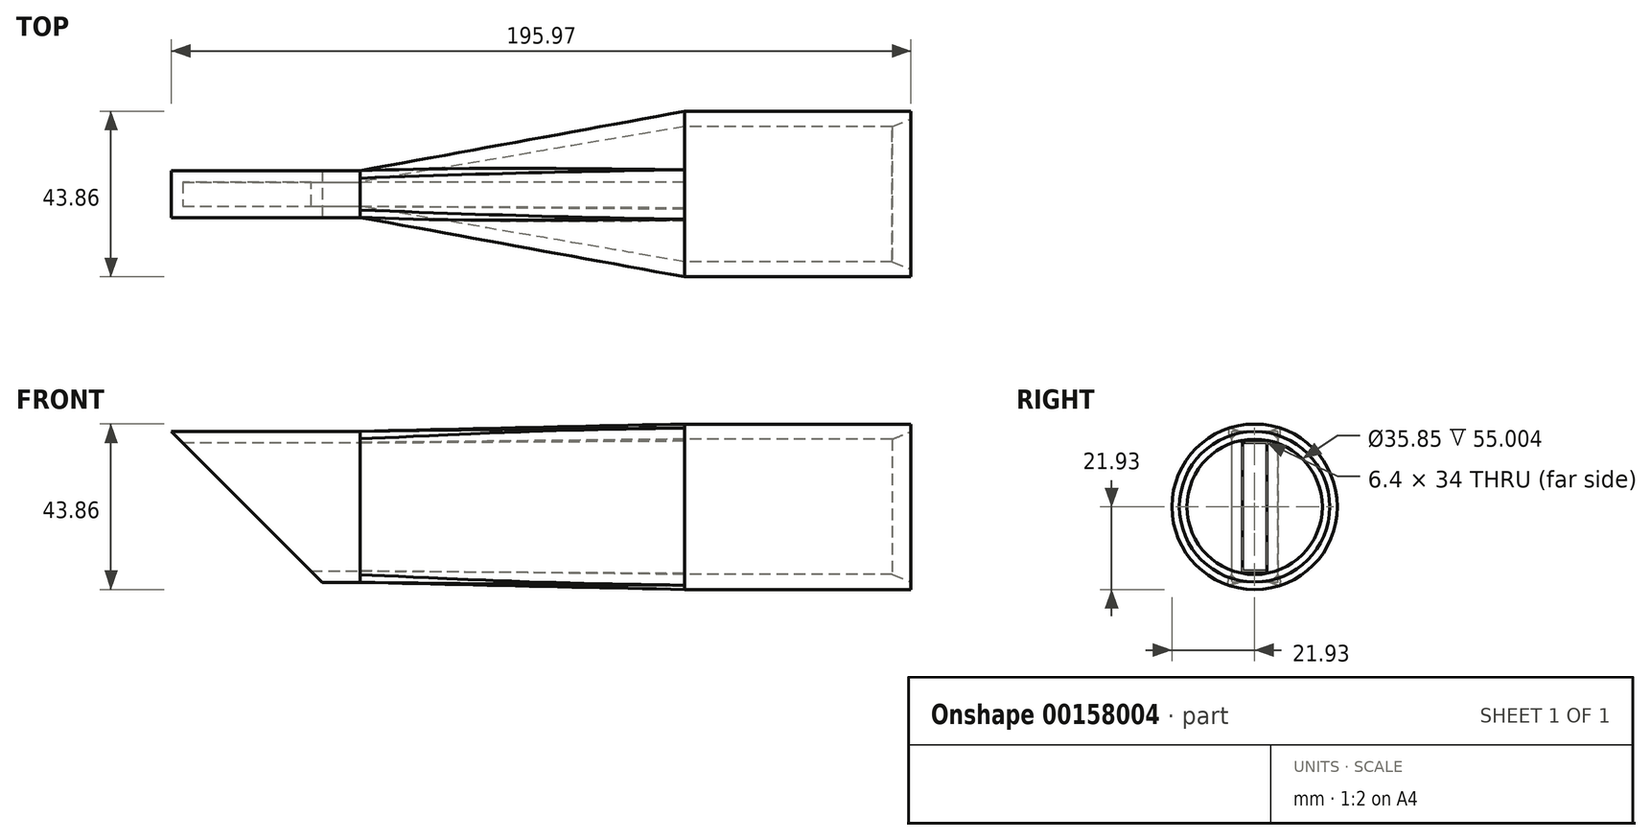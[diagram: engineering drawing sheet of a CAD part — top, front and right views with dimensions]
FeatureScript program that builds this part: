
annotation { "Feature Type Name" : "Feature", "Feature Type Description" : "" }
export const myFeature = defineFeature(function(context is Context, id is Id, definition is map)
    precondition{}
    {
        {
            var Q0;
            Q0=qCreatedBy(makeId("Front.planeOp"),FACE);
            var sketch = newSketch(context, id + "F0", { "sketchPlane" : qUnion([Q0])});
            skLineSegment(sketch, "E0", {"start": v(-54.03, 0) * mm, "end": v(-4.03, 0) * mm, "construction": true});
            skLineSegment(sketch, "E1", {"start": v(-4.03, 0) * mm, "end": v(-4.03, 17.93) * mm, "construction": true});
            skLineSegment(sketch, "E2", {"start": v(-54.04, 0.55) * mm, "end": v(-54.04, 17.93) * mm, "construction": true});
            skLineSegment(sketch, "E3", {"start": v(-54.04, 17.92) * mm, "end": v(5.97, 17.93) * mm});
            skLineSegment(sketch, "E4", {"start": v(-54.04, 17.93) * mm, "end": v(-54.04, 21.92) * mm});
            skLineSegment(sketch, "E5", {"start": v(5.97, 17.93) * mm, "end": v(5.97, 21.93) * mm});
            skLineSegment(sketch, "E6", {"start": v(5.97, 21.93) * mm, "end": v(-54.04, 21.92) * mm});
            skSolve(sketch);
        }
        {
            var Q0;
            Q0=makeQuery(id+"F0.imprint","IMPRINT",FACE,{"disambiguationData":[TD([[makeQuery(id+"F0.imprint","IMPRINT",EDGE,{"derivedFrom":sQuery(id+"F0.wireOp",EDGE,"E3")}),1.0]])]});
            var Q1;
            Q1=sQuery(id+"F0.wireOp",EDGE,"E0");
            revolve(context, id + "F1", {"entities" : qUnion([Q0]), "axis" : qUnion([Q1]), "revolveType" : RevolveType.FULL});
        }
        {
            var Q0;
            Q0=makeQuery(id+"F1.opRevolve","SWEPT_EDGE",EDGE,{"disambiguationData":[OSD([sQuery(id+"F0.wireOp",EDGE,"E3"),sQuery(id+"F0.wireOp",EDGE,"E5")])]});
            chamfer(context, id + "F2", {"entities" : qUnion([Q0]), "chamferType" : ChamferType.TWO_OFFSETS, "width1" : 2 * mm, "oppositeDirection" : false, "width2" : 5 * mm, "tangentPropagation" : true});
        }
        {
            var Q0;
            Q0=qCreatedBy(makeId("Right.planeOp"),FACE);
            cPlane(context, id + "F3", {"entities" : qUnion([Q0]), "cplaneType" : CPlaneType.OFFSET, "offset" : 140 * mm, "oppositeDirection" : true, "width" : 150 * mm, "height" : 150 * mm});
        }
        {
            var Q0;
            Q0=qCreatedBy(id+"F3.planeOp",FACE);
            var sketch = newSketch(context, id + "F4", { "sketchPlane" : qUnion([Q0])});
            skPoint(sketch, "E7.0", {"position": v(0, 0) * mm});
            skLineSegment(sketch, "E8.bottom", {"start": v(6.2, 20) * mm, "end": v(-6.2, 20) * mm});
            skLineSegment(sketch, "E8.top", {"start": v(6.2, -20) * mm, "end": v(-6.2, -20) * mm});
            skLineSegment(sketch, "E8.left", {"start": v(6.2, 20) * mm, "end": v(6.2, -20) * mm});
            skLineSegment(sketch, "E8.right", {"start": v(-6.2, 20) * mm, "end": v(-6.2, -20) * mm});
            skLineSegment(sketch, "E9.0", {"start": v(3.2, 17) * mm, "end": v(-3.2, 17) * mm});
            skLineSegment(sketch, "E9.1", {"start": v(3.2, 17) * mm, "end": v(3.2, -17) * mm});
            skLineSegment(sketch, "E9.2", {"start": v(3.2, -17) * mm, "end": v(-3.2, -17) * mm});
            skLineSegment(sketch, "E9.3", {"start": v(-3.2, 17) * mm, "end": v(-3.2, -17) * mm});
            skSolve(sketch);
        }
        {
            var Q0;
            Q0=makeQuery(id+"F1.opRevolve","SWEPT_FACE",FACE,{"disambiguationData":[OSD([sQuery(id+"F0.wireOp",EDGE,"E4")])]});
            var sketch = newSketch(context, id + "F5", { "sketchPlane" : qUnion([Q0])});
            skArc(sketch, "E10", {"start": v(-6.45, 20.96) * mm, "mid": v(-21.92, 0.06) * mm, "end": v(-6.57, -20.92) * mm});
            skArc(sketch, "E11", {"start": v(6.7, 20.88) * mm, "mid": v(0.13, 21.92) * mm, "end": v(-6.45, 20.96) * mm});
            skArc(sketch, "E12", {"start": v(-6.57, -20.92) * mm, "mid": v(0.26, -21.92) * mm, "end": v(7.06, -20.76) * mm});
            skArc(sketch, "E13", {"start": v(7.06, -20.76) * mm, "mid": v(21.92, 0.2) * mm, "end": v(6.7, 20.88) * mm});
            skArc(sketch, "E14", {"start": v(3.93, 17.49) * mm, "mid": v(0.31, 17.92) * mm, "end": v(-3.32, 17.62) * mm});
            skArc(sketch, "E15", {"start": v(-3.32, 17.62) * mm, "mid": v(-17.92, -0.02) * mm, "end": v(-3.28, -17.62) * mm});
            skArc(sketch, "E16", {"start": v(-3.28, -17.62) * mm, "mid": v(0.15, -17.92) * mm, "end": v(3.57, -17.57) * mm});
            skArc(sketch, "E17", {"start": v(3.57, -17.57) * mm, "mid": v(17.92, -0.19) * mm, "end": v(3.93, 17.49) * mm});
            skSolve(sketch);
        }
        {
            var Q0;
            Q0=makeQuery(id+"F4.imprint","IMPRINT",FACE,{"disambiguationData":[TD([[makeQuery(id+"F4.imprint","IMPRINT",EDGE,{"derivedFrom":sQuery(id+"F4.wireOp",EDGE,"E9.0")}),1.0]])]});
            var Q1;
            Q1=makeQuery(id+"F5.imprint","IMPRINT",FACE,{"disambiguationData":[TD([[makeQuery(id+"F5.imprint","IMPRINT",EDGE,{"derivedFrom":sQuery(id+"F5.wireOp",EDGE,"E14")}),1.0]])]});
            loft(context, id + "F6", {"sheetProfilesArray" : [{ "sheetProfileEntities" : qUnion([Q0]) }, { "sheetProfileEntities" : qUnion([Q1]) }]});
        }
        {
            var Q0;
            Q0=qCreatedBy(id+"F3.planeOp",FACE);
            var sketch = newSketch(context, id + "F7", { "sketchPlane" : qUnion([Q0])});
            skLineSegment(sketch, "E18.0", {"start": v(6.2, 20) * mm, "end": v(-6.2, 20) * mm});
            skLineSegment(sketch, "E19.0", {"start": v(6.2, 20) * mm, "end": v(6.2, -20) * mm});
            skLineSegment(sketch, "E20.0", {"start": v(-6.2, 20) * mm, "end": v(-6.2, -20) * mm});
            skLineSegment(sketch, "E21.0", {"start": v(6.2, -20) * mm, "end": v(-6.2, -20) * mm});
            skSolve(sketch);
        }
        {
            var Q0;
            Q0=makeQuery(id+"F5.imprint","IMPRINT",FACE,{"disambiguationData":[TD([[makeQuery(id+"F5.imprint","IMPRINT",EDGE,{"derivedFrom":sQuery(id+"F5.wireOp",EDGE,"E14")}),1.0]])]});
            var sketch = newSketch(context, id + "F8", { "sketchPlane" : qUnion([Q0])});
            skArc(sketch, "E22.0", {"start": v(-6.45, 20.96) * mm, "mid": v(-21.92, 0.06) * mm, "end": v(-6.57, -20.92) * mm});
            skArc(sketch, "E23.0", {"start": v(6.7, 20.88) * mm, "mid": v(0.13, 21.92) * mm, "end": v(-6.45, 20.96) * mm});
            skArc(sketch, "E24.0", {"start": v(7.06, -20.76) * mm, "mid": v(21.92, 0.2) * mm, "end": v(6.7, 20.88) * mm});
            skArc(sketch, "E25.0", {"start": v(-6.57, -20.92) * mm, "mid": v(0.26, -21.92) * mm, "end": v(7.06, -20.76) * mm});
            skSolve(sketch);
        }
        {
            var Q1;
            Q1=makeQuery(id+"F7.imprint","IMPRINT",FACE,{"disambiguationData":[TD([[makeQuery(id+"F7.imprint","IMPRINT",EDGE,{"derivedFrom":sQuery(id+"F7.wireOp",EDGE,"E18.0")}),1.0]])]});
            var Q2;
            Q2 = qSketchRegion(id + "F8", true);
            loft(context, id + "F9", {"sheetProfilesArray" : [{ "sheetProfileEntities" : qUnion([Q1]) }, { "sheetProfileEntities" : qUnion([Q2]) }]});
        }
        {
            var Q0;
            Q0=makeQuery(id+"F6.opLoft","SWEPT_BODY",BODY,{"disambiguationData":[OSD([makeQuery(id+"F4.imprint","IMPRINT",FACE,{"disambiguationData":[TD([[makeQuery(id+"F4.imprint","IMPRINT",EDGE,{"derivedFrom":sQuery(id+"F4.wireOp",EDGE,"E9.0")}),1.0]])]}),makeQuery(id+"F5.imprint","IMPRINT",FACE,{"disambiguationData":[TD([[makeQuery(id+"F5.imprint","IMPRINT",EDGE,{"derivedFrom":sQuery(id+"F5.wireOp",EDGE,"E14")}),1.0]])]})])]});
            var Q1;
            Q1=makeQuery(id+"F9.opLoft","SWEPT_BODY",BODY,{"disambiguationData":[OSD([makeQuery(id+"F7.imprint","IMPRINT",FACE,{"disambiguationData":[TD([[makeQuery(id+"F7.imprint","IMPRINT",EDGE,{"derivedFrom":sQuery(id+"F7.wireOp",EDGE,"E18.0")}),1.0]])]}),makeQuery(id+"F8.imprint","IMPRINT",FACE,{"disambiguationData":[TD([[makeQuery(id+"F8.imprint","IMPRINT",EDGE,{"derivedFrom":sQuery(id+"F8.wireOp",EDGE,"E22.0")}),1.0]])]})])]});
            booleanBodies(context, id + "F10", {"operationType" : BooleanOperationType.SUBTRACTION, "tools" : qUnion([Q0]), "targets" : qUnion([Q1])});
        }
        {
            var Q0;
            Q0=makeQuery(id+"F9.opLoft","CAP_FACE",FACE,{"disambiguationData":[OSD([makeQuery(id+"F7.imprint","IMPRINT",FACE,{"disambiguationData":[TD([[makeQuery(id+"F7.imprint","IMPRINT",EDGE,{"derivedFrom":sQuery(id+"F7.wireOp",EDGE,"E18.0")}),1.0]])]})])],"isStart":true});
            extrude(context, id + "F11", {"entities" : qUnion([Q0]), "depth" : 50 * mm});
        }
        {
            var Q0;
            Q0=makeQuery(id+"F11.opExtrude","SWEPT_FACE",FACE,{"disambiguationData":[OSD([sQuery(id+"F7.wireOp",EDGE,"E18.0"),sQuery(id+"F7.wireOp",EDGE,"E20.0"),sQuery(id+"F7.wireOp",EDGE,"E21.0")])]});
            var sketch = newSketch(context, id + "F12", { "sketchPlane" : qUnion([Q0])});
            skLineSegment(sketch, "E26.0", {"start": v(-190, 20) * mm, "end": v(-190, -20) * mm});
            skFitSpline(sketch, "E27.0", {"points": [v(-210, 20) * mm, v(-193.33, 20) * mm, v(-176.67, 20) * mm, v(-160, 20) * mm]});
            skFitSpline(sketch, "E28.0", {"points": [v(-210, -20) * mm, v(-193.33, -20) * mm, v(-176.67, -20) * mm, v(-160, -20) * mm]});
            skLineSegment(sketch, "E29", {"start": v(-190, 20) * mm, "end": v(-150, -20) * mm});
            skSolve(sketch);
        }
        {
            var Q0;
            {var subQ0=sQuery(id+"F12.wireOp",EDGE,"E26.0");Q0=makeQuery(id+"F12.imprint","IMPRINT",FACE,{"disambiguationData":[TD([[makeQuery(id+"F12.imprint","IMPRINT",EDGE,{"derivedFrom":subQ0}),1.0]])]});}
            extrude(context, id + "F13", {"entities" : qUnion([Q0]), "operationType" : NewBodyOperationType.REMOVE, "oppositeDirection" : true, "depth" : 25 * mm, "symmetric" : true});
        }
        {
            var Q0;
            Q0=makeQuery(id+"F13.boolean.opBoolean","MERGE",EDGE,{"derivedFrom":[makeQuery(id+"F11.opExtrude","CAP_EDGE",EDGE,{"disambiguationData":[OSD([sQuery(id+"F7.wireOp",EDGE,"E18.0"),sQuery(id+"F7.wireOp",EDGE,"E19.0"),sQuery(id+"F7.wireOp",EDGE,"E20.0")])],"isStart":false}),makeQuery(id+"F13.opExtrude","SWEPT_EDGE",EDGE,{"disambiguationData":[OSD([sQuery(id+"F12.wireOp",EDGE,"E26.0"),sQuery(id+"F12.wireOp",EDGE,"E27.0"),sQuery(id+"F12.wireOp",EDGE,"E29")])]})]});
            var Q1;
            Q1=makeQuery(id+"F13.boolean.opBoolean","INTERSECT",EDGE,{"derivedFrom":[makeQuery(id+"F11.opExtrude","SWEPT_FACE",FACE,{"disambiguationData":[OSD([sQuery(id+"F7.wireOp",EDGE,"E18.0"),sQuery(id+"F7.wireOp",EDGE,"E19.0"),sQuery(id+"F7.wireOp",EDGE,"E21.0")])]}),makeQuery(id+"F13.opExtrude","SWEPT_FACE",FACE,{"disambiguationData":[OSD([sQuery(id+"F12.wireOp",EDGE,"E29")])]})]});
            var Q2;
            Q2=makeQuery(id+"F13.boolean.opBoolean","COPY",EDGE,{"derivedFrom":makeQuery(id+"F13.opExtrude","SWEPT_EDGE",EDGE,{"disambiguationData":[OSD([sQuery(id+"F12.wireOp",EDGE,"E28.0"),sQuery(id+"F12.wireOp",EDGE,"E29")])]})});
            var Q3;
            Q3=makeQuery(id+"F13.boolean.opBoolean","INTERSECT",EDGE,{"derivedFrom":[makeQuery(id+"F11.opExtrude","SWEPT_FACE",FACE,{"disambiguationData":[OSD([sQuery(id+"F7.wireOp",EDGE,"E18.0"),sQuery(id+"F7.wireOp",EDGE,"E20.0"),sQuery(id+"F7.wireOp",EDGE,"E21.0")])]}),makeQuery(id+"F13.opExtrude","SWEPT_FACE",FACE,{"disambiguationData":[OSD([sQuery(id+"F12.wireOp",EDGE,"E29")])]})]});
            var Q4;
            Q4=makeQuery(id+"F13.boolean.opBoolean","INTERSECT",EDGE,{"derivedFrom":[makeQuery(id+"F11.opExtrude","SWEPT_FACE",FACE,{"disambiguationData":[OSD([sQuery(id+"F4.wireOp",EDGE,"E9.0"),sQuery(id+"F4.wireOp",EDGE,"E9.1"),sQuery(id+"F4.wireOp",EDGE,"E9.2")])]}),makeQuery(id+"F13.opExtrude","SWEPT_FACE",FACE,{"disambiguationData":[OSD([sQuery(id+"F12.wireOp",EDGE,"E29")])]})]});
            var Q5;
            Q5=makeQuery(id+"F13.boolean.opBoolean","INTERSECT",EDGE,{"derivedFrom":[makeQuery(id+"F11.opExtrude","SWEPT_FACE",FACE,{"disambiguationData":[OSD([sQuery(id+"F4.wireOp",EDGE,"E9.0"),sQuery(id+"F4.wireOp",EDGE,"E9.1"),sQuery(id+"F4.wireOp",EDGE,"E9.3")])]}),makeQuery(id+"F13.opExtrude","SWEPT_FACE",FACE,{"disambiguationData":[OSD([sQuery(id+"F12.wireOp",EDGE,"E29")])]})]});
            var Q6;
            Q6=makeQuery(id+"F13.boolean.opBoolean","INTERSECT",EDGE,{"derivedFrom":[makeQuery(id+"F11.opExtrude","SWEPT_FACE",FACE,{"disambiguationData":[OSD([sQuery(id+"F4.wireOp",EDGE,"E9.0"),sQuery(id+"F4.wireOp",EDGE,"E9.2"),sQuery(id+"F4.wireOp",EDGE,"E9.3")])]}),makeQuery(id+"F13.opExtrude","SWEPT_FACE",FACE,{"disambiguationData":[OSD([sQuery(id+"F12.wireOp",EDGE,"E29")])]})]});
            var Q7;
            Q7=makeQuery(id+"F13.boolean.opBoolean","INTERSECT",EDGE,{"derivedFrom":[makeQuery(id+"F11.opExtrude","SWEPT_FACE",FACE,{"disambiguationData":[OSD([sQuery(id+"F4.wireOp",EDGE,"E9.1"),sQuery(id+"F4.wireOp",EDGE,"E9.2"),sQuery(id+"F4.wireOp",EDGE,"E9.3")])]}),makeQuery(id+"F13.opExtrude","SWEPT_FACE",FACE,{"disambiguationData":[OSD([sQuery(id+"F12.wireOp",EDGE,"E29")])]})]});
            var Q8;
            Q8=makeQuery(id+"F11.opExtrude","SWEPT_EDGE",EDGE,{"disambiguationData":[OSD([sQuery(id+"F7.wireOp",EDGE,"E18.0"),sQuery(id+"F7.wireOp",EDGE,"E19.0")])]});
            var Q9;
            Q9=makeQuery(id+"F11.opExtrude","SWEPT_EDGE",EDGE,{"disambiguationData":[OSD([sQuery(id+"F7.wireOp",EDGE,"E18.0"),sQuery(id+"F7.wireOp",EDGE,"E20.0")])]});
            var Q10;
            Q10=makeQuery(id+"F11.opExtrude","SWEPT_EDGE",EDGE,{"disambiguationData":[OSD([sQuery(id+"F7.wireOp",EDGE,"E19.0"),sQuery(id+"F7.wireOp",EDGE,"E21.0")])]});
            var Q11;
            Q11=makeQuery(id+"F11.opExtrude","SWEPT_EDGE",EDGE,{"disambiguationData":[OSD([sQuery(id+"F7.wireOp",EDGE,"E20.0"),sQuery(id+"F7.wireOp",EDGE,"E21.0")])]});
            var Q12;
            Q12=makeQuery(id+"F9.opLoft","SWEPT_EDGE",EDGE,{"disambiguationData":[OSD([sQuery(id+"F7.wireOp",EDGE,"E19.0"),sQuery(id+"F7.wireOp",EDGE,"E21.0"),sQuery(id+"F8.wireOp",EDGE,"E22.0"),sQuery(id+"F8.wireOp",EDGE,"E25.0")])]});
            var Q13;
            Q13=makeQuery(id+"F9.opLoft","SWEPT_EDGE",EDGE,{"disambiguationData":[OSD([sQuery(id+"F7.wireOp",EDGE,"E20.0"),sQuery(id+"F7.wireOp",EDGE,"E21.0"),sQuery(id+"F8.wireOp",EDGE,"E24.0"),sQuery(id+"F8.wireOp",EDGE,"E25.0")])]});
            var Q14;
            Q14=makeQuery(id+"F9.opLoft","SWEPT_EDGE",EDGE,{"disambiguationData":[OSD([sQuery(id+"F7.wireOp",EDGE,"E18.0"),sQuery(id+"F7.wireOp",EDGE,"E19.0"),sQuery(id+"F8.wireOp",EDGE,"E22.0"),sQuery(id+"F8.wireOp",EDGE,"E23.0")])]});
            var Q15;
            Q15=makeQuery(id+"F9.opLoft","SWEPT_EDGE",EDGE,{"disambiguationData":[OSD([sQuery(id+"F7.wireOp",EDGE,"E18.0"),sQuery(id+"F7.wireOp",EDGE,"E20.0"),sQuery(id+"F8.wireOp",EDGE,"E23.0"),sQuery(id+"F8.wireOp",EDGE,"E24.0")])]});
            chamfer(context, id + "F14", {"entities" : qUnion([Q0, Q1, Q2, Q3, Q4, Q5, Q6, Q7, Q8, Q9, Q10, Q11, Q12, Q13, Q14, Q15]), "width" : 2 * mm, "tangentPropagation" : true});
        }
    });
